# Revit family: STS-483 IP-терминал биометрической идентификации_RV17_LOD400 (0712..23)
name_source: partatom
category: Датчики
revit_build: Autodesk Revit 2017 (Build: 20170118_1100(x64)
units: mm (PartAtom-declared; Revit-internal decimal feet)

## family parameters
Всегда вертикально = Нет
На основе рабочей плоскости = Нет
Общий = Нет
При загрузке вырезать с полостями = Нет
Размер круглого соединителя = Использовать диаметр
Сохранять ориентацию аннотаций = Нет
Тип детали = Нормальный
Точка расчета площади = Нет

## types (1)
- STS-483
    ADSK_URL страницы изделия = https://stilsoft.ru
    ADSK_Единица измерения = шт.
    ADSK_Завод-изготовитель = ООО «Основа Безопасности»
    ADSK_Количество = 1
    ADSK_Марка = СТВФ.425728.021
    ADSK_Масса = 1.5
    ADSK_Наименование = IP-терминал биометрической идентификации STS-483
    ADSK_Размер_Высота = 25 мм
    ADSK_Размер_Длина = 250 мм
    ADSK_Размер_Ширина = 130 мм
    d_короба = 20 мм
    Встроенная видеокамера = Цветная
    Встроенная память, ГБ = 4
    Диапазон рабочих температур, °С = от -40 до +50
    Интерфейс связи = 100
М Ethernet
    Интерфейсы = Wiegand 26 RS-485, RS-232
    Матрица = 1/2.8 CMOS
    Мощность = 2
    Напряжение = 12
    Пиковая потребляемая мощность, Вт = 8
    Поддержка карты памяти TF, до, ГБ = 128
    Размер дисплея, дюйм = 8
    Разрешение видеокамеры, пикс. = 1080х1920
    Режим работы = непрерывный
    Скорость распознавания, мс = 0.2
    Степень защиты от внешних воздействий = IP65
